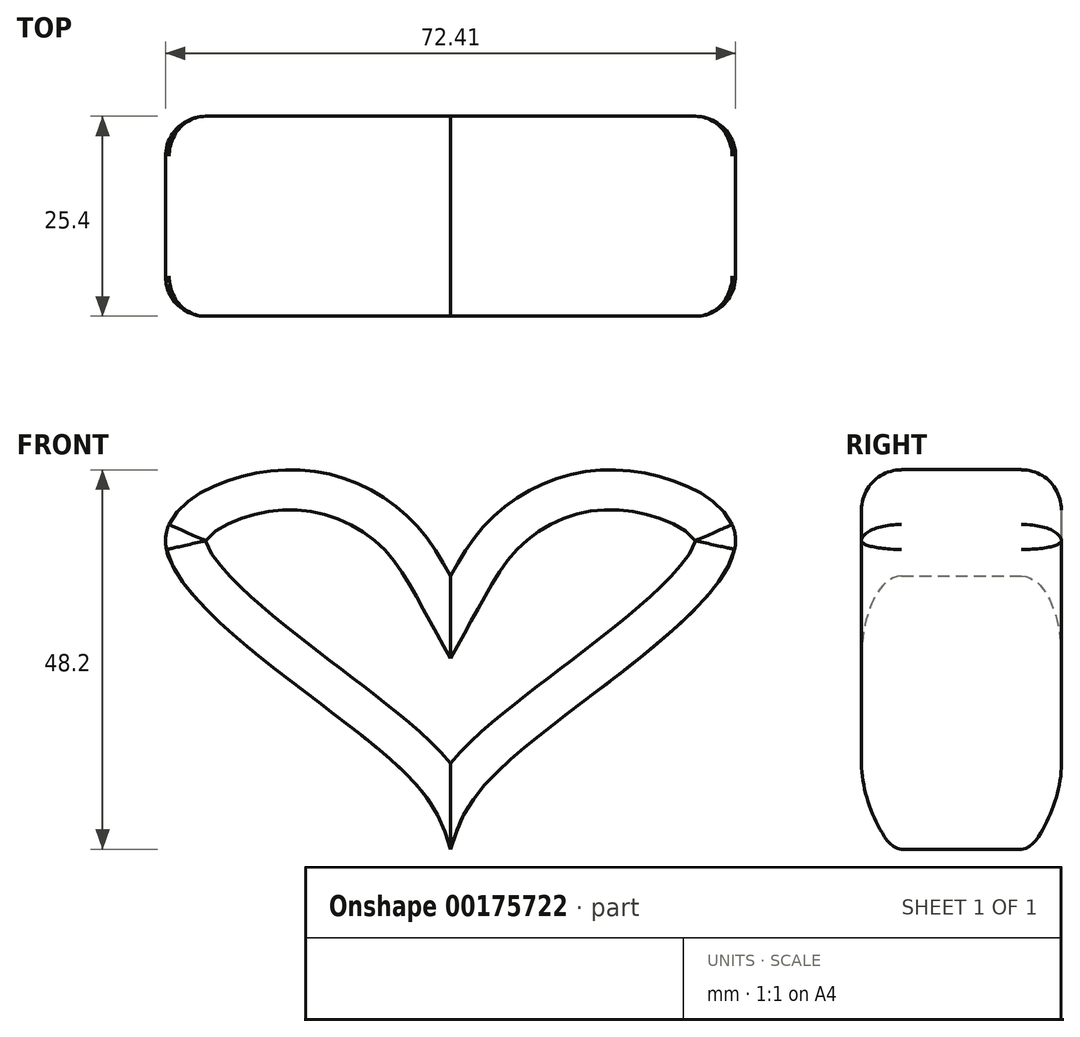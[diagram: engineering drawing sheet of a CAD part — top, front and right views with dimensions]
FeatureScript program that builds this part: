
annotation { "Feature Type Name" : "Feature", "Feature Type Description" : "" }
export const myFeature = defineFeature(function(context is Context, id is Id, definition is map)
    precondition{}
    {
        {
            var Q0;
            Q0=qCreatedBy(makeId("Front.planeOp"),FACE);
            var sketch = newSketch(context, id + "F0", { "sketchPlane" : qUnion([Q0])});
            skLineSegment(sketch, "E0", {"start": v(-72.61, 41.35) * mm, "end": v(-72.61, 6.64) * mm});
            skFitSpline(sketch, "E1", {"points": [v(-72.61, 41.35) * mm, v(-70.67, 44.64) * mm, v(-65.88, 50.02) * mm, v(-51.07, 54.8) * mm, v(-36.41, 45.53) * mm, v(-66.18, 16.96) * mm, v(-72.61, 6.64) * mm], "startDerivative": vector(20.22, 36.43) * mm, "endDerivative": vector(-18.05, -58.53) * mm});
            skFitSpline(sketch, "E2.MirrorCS", {"points": [v(-72.61, 41.35) * mm, v(-74.56, 44.64) * mm, v(-79.34, 50.02) * mm, v(-94.15, 54.8) * mm, v(-108.81, 45.53) * mm, v(-79.04, 16.96) * mm, v(-72.61, 6.64) * mm], "startDerivative": vector(-20.22, 36.43) * mm, "endDerivative": vector(18.05, -58.53) * mm});
            skSolve(sketch);
        }
        {
            var Q0;
            Q0 = qSketchRegion(id + "F0", true);
            extrude(context, id + "F1", {"entities" : qUnion([Q0]), "endBound" : BoundingType.SYMMETRIC, "depth" : 25.4 * mm});
        }
        {
            var Q0;
            Q0=makeQuery(id+"F1.opExtrude","CAP_FACE",FACE,{"disambiguationData":[OSD([sQuery(id+"F0.wireOp",EDGE,"E1"),sQuery(id+"F0.wireOp",EDGE,"E2.MirrorCS")])],"isStart":true});
            fillet(context, id + "F2", {"entities" : qUnion([Q0]), "radius" : 5.08 * mm, "tangentPropagation" : true, "allowEdgeOverflow" : false});
        }
        {
            var Q0;
            Q0=makeQuery(id+"F1.opExtrude","CAP_FACE",FACE,{"disambiguationData":[OSD([sQuery(id+"F0.wireOp",EDGE,"E1"),sQuery(id+"F0.wireOp",EDGE,"E2.MirrorCS")])],"isStart":false});
            fillet(context, id + "F3", {"entities" : qUnion([Q0]), "radius" : 5.08 * mm, "tangentPropagation" : true, "allowEdgeOverflow" : false});
        }
    });
